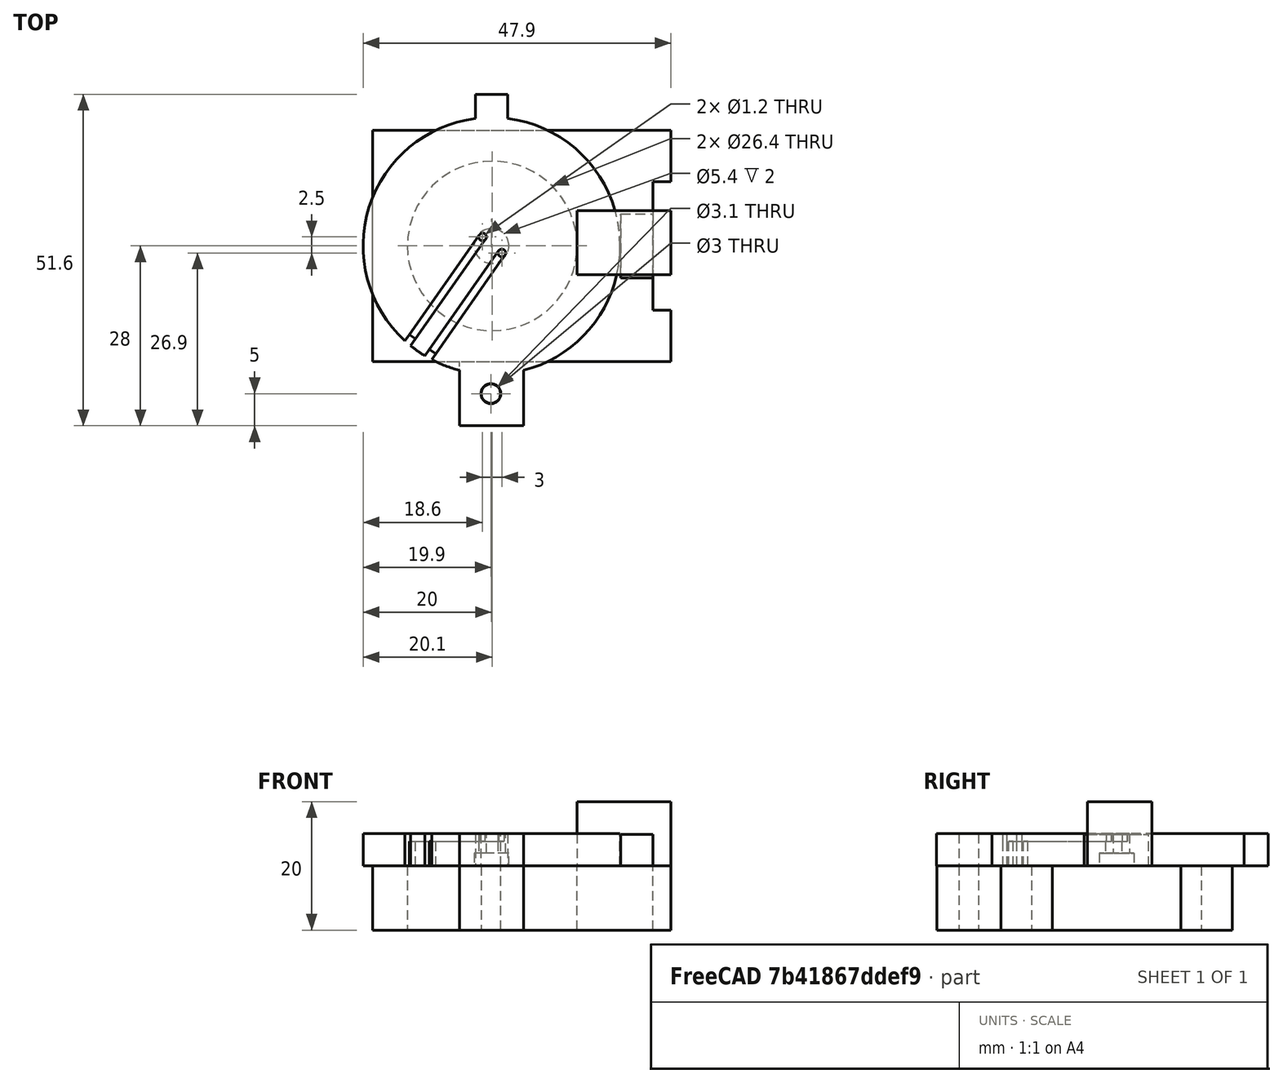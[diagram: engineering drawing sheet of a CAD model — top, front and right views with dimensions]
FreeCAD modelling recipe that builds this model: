
FCSTD DOCUMENT  (FreeCAD 1.0R39319 (Git))
Label: CdSHolderBooleaned
License: All rights reserved
LicenseURL: https://en.wikipedia.org/wiki/All_rights_reserved
objects: Part::Box×11, Part::Cut×11, Part::Cylinder×7, Part::Fuse×4
note: 33 computed .brp shape members not serialized (recipe doc carries the construction recipe); baked Part::Feature solids carry a one-line shape summary decoded from their .brp

FEATURE [Part::Cylinder] Cylinder  label="cardboardBarrelHolder"
  Angle = 360
  AttacherType = Attacher::AttachEngine3D
  FirstAngle = 0
  Height = 40
  Placement = pos=(-1.1,0,-20) rot=(0,0,1;0rad)
  Radius = 13.2
  SecondAngle = 0
FEATURE [Part::Box] Box  label="mainPiece"
  AttacherType = Attacher::AttachEngine3D
  Height = 46.4
  Length = 10
  Placement = pos=(-19.7,-18,-4.4e-15) rot=(0,1,0;1.5708rad)
  Width = 36
FEATURE [Part::Box] Box001  label="Cube001"
  AttacherType = Attacher::AttachEngine3D
  Height = 14.6
  Length = 10
  Placement = pos=(12.1,-4.5,10) rot=(0,1,0;1.5708rad)
  Width = 10
FEATURE [Part::Box] Box002  label="hingePinTab"
  AttacherType = Attacher::AttachEngine3D
  Height = 10
  Length = 10
  Placement = pos=(-6.2,-27.952,-10) rot=(0,0,1;0rad)
  Width = 10
FEATURE [Part::Cylinder] Cylinder001  label="hingeTabHole"
  Angle = 360
  AttacherType = Attacher::AttachEngine3D
  FirstAngle = 0
  Height = 30
  Placement = pos=(-1.3,-23,-12) rot=(0,0,1;0rad)
  Radius = 1.5
  SecondAngle = 0
FEATURE [Part::Cylinder] Cylinder002  label="shutter"
  Angle = 360
  AttacherType = Attacher::AttachEngine3D
  FirstAngle = 0
  Height = 5
  Placement = pos=(-1.2,0,0) rot=(0,0,1;0rad)
  Radius = 20
  SecondAngle = 0
FEATURE [Part::Box] Box003  label="shutterHingeTab"
  AttacherType = Attacher::AttachEngine3D
  Height = 5
  Length = 10
  Placement = pos=(-6.2,-28,0) rot=(0,0,1;0rad)
  Width = 14
FEATURE [Part::Box] Box004  label="swivelStop"
  AttacherType = Attacher::AttachEngine3D
  Height = 5
  Length = 5
  Placement = pos=(18.9,-5,-0.1) rot=(0,0,1;0rad)
  Width = 10
FEATURE [Part::Box] Box005  label="footCutout"
  AttacherType = Attacher::AttachEngine3D
  Height = 20
  Length = 10
  Placement = pos=(23.9,-10,-18) rot=(0,0,1;0rad)
  Width = 20
FEATURE [Part::Cylinder] Cylinder003  label="shutterTabHole"
  Angle = 360
  AttacherType = Attacher::AttachEngine3D
  FirstAngle = 0
  Height = 50
  Placement = pos=(-1.3,-23,-12) rot=(0,0,1;0rad)
  Radius = 1.55
  SecondAngle = 0
FEATURE [Part::Box] Box006  label="shutterMoveTab"
  AttacherType = Attacher::AttachEngine3D
  Height = 5
  Length = 5
  Placement = pos=(-3.7,18.6,0) rot=(0,0,1;0rad)
  Width = 5
FEATURE [Part::Cylinder] Cylinder004  label="CdSDivot"
  Angle = 360
  AttacherType = Attacher::AttachEngine3D
  FirstAngle = 0
  Height = 10
  Placement = pos=(-1.2,0,-8) rot=(0,0,1;0rad)
  Radius = 2.7
  SecondAngle = 0
FEATURE [Part::Cylinder] Cylinder005  label="CdSWire1"
  Angle = 360
  AttacherType = Attacher::AttachEngine3D
  FirstAngle = 0
  Height = 30
  Placement = pos=(0.4,-1.1,-18) rot=(0,0,1;0rad)
  Radius = 0.6
  SecondAngle = 0
FEATURE [Part::Cylinder] Cylinder006  label="CdsWire2"
  Angle = 360
  AttacherType = Attacher::AttachEngine3D
  FirstAngle = 0
  Height = 30
  Placement = pos=(-2.6,1.4,-18) rot=(0,0,1;0rad)
  Radius = 0.6
  SecondAngle = 0
FEATURE [Part::Box] Box007  label="radialTransit1"
  AttacherType = Attacher::AttachEngine3D
  Height = 10
  Length = 1.2
  Placement = pos=(-17.353,-25.3595,3.8) rot=(0,0,1;5.67232rad)
  Width = 30
FEATURE [Part::Box] Box008  label="radialTransit2"
  AttacherType = Attacher::AttachEngine3D
  Height = 10
  Length = 1.2
  Placement = pos=(-20.3756,-22.8768,3.8) rot=(0,0,1;5.67232rad)
  Width = 30
FEATURE [Part::Box] Box009  label="radialTransit3"
  AttacherType = Attacher::AttachEngine3D
  Height = 10
  Length = 1.2
  Placement = pos=(-10.8716,-16.103,-4.1) rot=(-0.913318,0.287968,0.287968;4.62184rad)
  Width = 30
FEATURE [Part::Box] Box010  label="radialTransit4"
  AttacherType = Attacher::AttachEngine3D
  Height = 10
  Length = 1.2
  Placement = pos=(-14.0089,-13.7842,-4.1) rot=(-0.913318,0.287968,0.287968;4.62184rad)
  Width = 30
FEATURE [Part::Cut] Cut
  Base = -> Box
  Tool = -> Cylinder
FEATURE [Part::Cut] Cut001  label="mainPiece1"
  Base = -> Cut
  Tool = -> Box005
FEATURE [Part::Cut] Cut002
  Base = -> Cylinder002
  Tool = -> Cylinder004
FEATURE [Part::Cut] Cut003
  Base = -> Cut002
  Tool = -> Cylinder005
FEATURE [Part::Cut] Cut004
  Base = -> Cut003
  Tool = -> Cylinder006
FEATURE [Part::Cut] Cut005
  Base = -> Cut004
  Tool = -> Box007
FEATURE [Part::Cut] Cut006
  Base = -> Cut005
  Tool = -> Box008
FEATURE [Part::Cut] Cut007
  Base = -> Cut006
  Tool = -> Box009
FEATURE [Part::Cut] Cut008  label="shutter1"
  Base = -> Cut007
  Tool = -> Box010
FEATURE [Part::Cut] Cut009  label="shutterHingeTab001"
  Base = -> Box003
  Tool = -> Cylinder003
FEATURE [Part::Cut] Cut010  label="mainPieceHingeTab"
  Base = -> Box002
  Tool = -> Cylinder001
FEATURE [Part::Fuse] Fusion  label="mainPiece2"
  Base = -> Cut001
  Tool = -> Cut010
FEATURE [Part::Fuse] Fusion001  label="shutter2"
  Base = -> Cut008
  Tool = -> Cut009
FEATURE [Part::Fuse] Fusion002  label="mainPiece3"
  Base = -> Cut001
  Tool = -> Box004
FEATURE [Part::Fuse] Fusion003  label="shutter4"
  Base = -> Fusion001
  Tool = -> Box006
